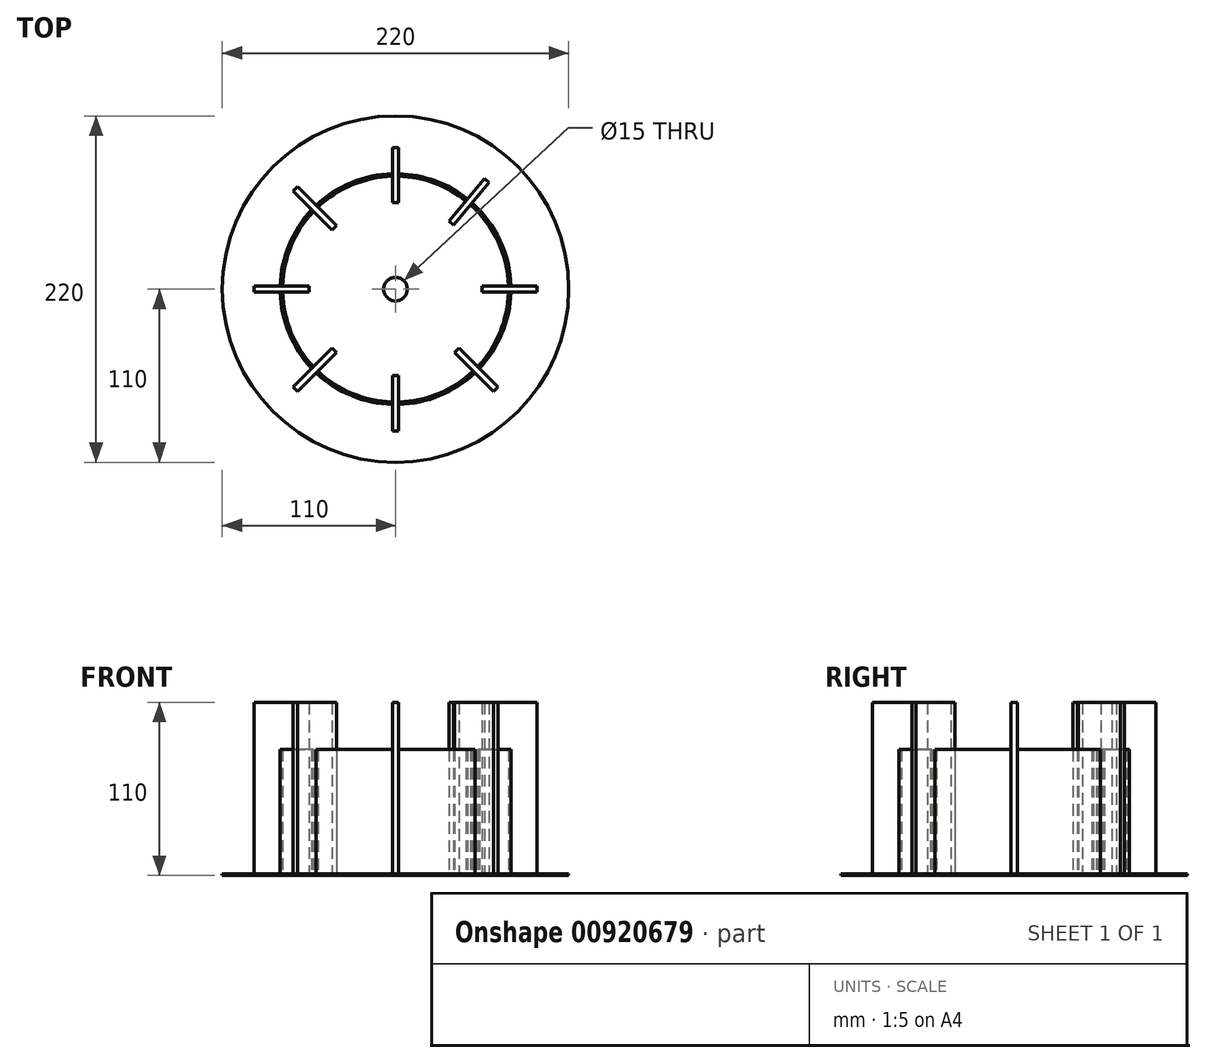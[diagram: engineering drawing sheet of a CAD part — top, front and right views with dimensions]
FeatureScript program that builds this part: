
annotation { "Feature Type Name" : "Feature", "Feature Type Description" : "" }
export const myFeature = defineFeature(function(context is Context, id is Id, definition is map)
    precondition{}
    {
        {
            var Q0;
            Q0=qCreatedBy(makeId("Top.planeOp"),FACE);
            var sketch = newSketch(context, id + "F0", { "sketchPlane" : qUnion([Q0])});
            skCircle(sketch, "E0", {"center": v(0, 0) * mm, "radius": 110 * mm});
            skCircle(sketch, "E1", {"center": v(0, 0) * mm, "radius": 7.5 * mm});
            skLineSegment(sketch, "E2", {"start": v(0, 0) * mm, "end": v(-55, 0) * mm, "construction": true});
            skLineSegment(sketch, "E3", {"start": v(0, 0) * mm, "end": v(55, 0) * mm, "construction": true});
            skLineSegment(sketch, "E4", {"start": v(0, 0) * mm, "end": v(0, -55) * mm, "construction": true});
            skLineSegment(sketch, "E5", {"start": v(0, 0) * mm, "end": v(0, 55) * mm, "construction": true});
            skLineSegment(sketch, "E6", {"start": v(0, 0) * mm, "end": v(-38.9, 38.9) * mm, "construction": true});
            skLineSegment(sketch, "E7", {"start": v(0, 0) * mm, "end": v(3, 3) * mm});
            skLineSegment(sketch, "E8", {"start": v(0, 0) * mm, "end": v(35.45, 42.05) * mm, "construction": true});
            skLineSegment(sketch, "E9", {"start": v(0, 0) * mm, "end": v(38.9, -38.9) * mm, "construction": true});
            skLineSegment(sketch, "E10", {"start": v(0, 0) * mm, "end": v(-38.9, -38.9) * mm, "construction": true});
            skCircle(sketch, "E11", {"center": v(0, 0) * mm, "radius": 55 * mm, "construction": true});
            skCircle(sketch, "E12", {"center": v(0, 0) * mm, "radius": 72.5 * mm, "construction": true});
            skPoint(sketch, "E13", {"position": v(-51.27, 51.27) * mm});
            skPoint(sketch, "E14", {"position": v(0, 72.5) * mm});
            skPoint(sketch, "E15", {"position": v(46.72, 55.44) * mm});
            skPoint(sketch, "E16", {"position": v(72.5, 0) * mm});
            skPoint(sketch, "E17", {"position": v(51.27, -51.27) * mm});
            skPoint(sketch, "E18", {"position": v(0, -72.5) * mm});
            skPoint(sketch, "E19", {"position": v(-51.27, -51.27) * mm});
            skPoint(sketch, "E20", {"position": v(-72.5, 0) * mm});
            skLineSegment(sketch, "E21", {"start": v(-38.9, -38.9) * mm, "end": v(-63.64, -63.64) * mm, "construction": true});
            skLineSegment(sketch, "E22", {"start": v(-63.64, -63.64) * mm, "end": v(-98.46, -98.46) * mm, "construction": true});
            skLineSegment(sketch, "E23", {"start": v(0, -55) * mm, "end": v(0, -90) * mm, "construction": true});
            skLineSegment(sketch, "E24", {"start": v(0, -90) * mm, "end": v(0, -139.25) * mm, "construction": true});
            skLineSegment(sketch, "E25", {"start": v(38.9, -38.9) * mm, "end": v(63.64, -63.64) * mm, "construction": true});
            skLineSegment(sketch, "E26", {"start": v(63.64, -63.64) * mm, "end": v(98.46, -98.46) * mm, "construction": true});
            skLineSegment(sketch, "E27", {"start": v(90, 0) * mm, "end": v(139.25, 0) * mm, "construction": true});
            skLineSegment(sketch, "E28", {"start": v(55, 0) * mm, "end": v(90, 0) * mm, "construction": true});
            skLineSegment(sketch, "E29", {"start": v(58, 68.82) * mm, "end": v(89.74, 106.47) * mm, "construction": true});
            skLineSegment(sketch, "E30", {"start": v(35.45, 42.05) * mm, "end": v(58, 68.82) * mm, "construction": true});
            skLineSegment(sketch, "E31", {"start": v(0, 55) * mm, "end": v(0, 55) * mm});
            skLineSegment(sketch, "E32", {"start": v(0, 90) * mm, "end": v(0, 90) * mm});
            skArc(sketch, "E33", {"start": v(-63.64, 63.64) * mm, "mid": v(34.44, -83.15) * mm, "end": v(0, 90) * mm, "construction": true});
            skLineSegment(sketch, "E34", {"start": v(-38.9, 38.9) * mm, "end": v(-38.9, 38.9) * mm});
            skLineSegment(sketch, "E35", {"start": v(-90, 0) * mm, "end": v(-139.25, 0) * mm, "construction": true});
            skLineSegment(sketch, "E36", {"start": v(-55, 0) * mm, "end": v(-90, 0) * mm, "construction": true});
            skLineSegment(sketch, "E37.0", {"start": v(-55, 2) * mm, "end": v(-90, 2) * mm});
            skLineSegment(sketch, "E38.0", {"start": v(-55, -2) * mm, "end": v(-90, -2) * mm});
            skLineSegment(sketch, "E39", {"start": v(-63.64, 63.64) * mm, "end": v(-63.64, 63.64) * mm});
            skLineSegment(sketch, "E40", {"start": v(-38.9, 38.9) * mm, "end": v(-63.64, 63.64) * mm, "construction": true});
            skLineSegment(sketch, "E41", {"start": v(-63.64, 63.64) * mm, "end": v(-98.46, 98.46) * mm, "construction": true});
            skLineSegment(sketch, "E42.0", {"start": v(-37.48, 40.3) * mm, "end": v(-62.23, 65.05) * mm});
            skLineSegment(sketch, "E43.0", {"start": v(-40.3, 37.48) * mm, "end": v(-65.05, 62.23) * mm});
            skLineSegment(sketch, "E44.0", {"start": v(36.98, 40.77) * mm, "end": v(59.53, 67.53) * mm});
            skLineSegment(sketch, "E45.0", {"start": v(33.92, 43.34) * mm, "end": v(56.47, 70.1) * mm});
            skLineSegment(sketch, "E46.0", {"start": v(55, -2) * mm, "end": v(90, -2) * mm});
            skLineSegment(sketch, "E47.0", {"start": v(55, 2) * mm, "end": v(90, 2) * mm});
            skLineSegment(sketch, "E48.0", {"start": v(37.48, -40.3) * mm, "end": v(62.23, -65.05) * mm});
            skLineSegment(sketch, "E49.0", {"start": v(40.3, -37.48) * mm, "end": v(65.05, -62.23) * mm});
            skLineSegment(sketch, "E50.0", {"start": v(-2, -55) * mm, "end": v(-2, -90) * mm});
            skLineSegment(sketch, "E51.0", {"start": v(2, -55) * mm, "end": v(2, -90) * mm});
            skLineSegment(sketch, "E52.0", {"start": v(-40.3, -37.48) * mm, "end": v(-65.05, -62.23) * mm});
            skLineSegment(sketch, "E53.0", {"start": v(-37.48, -40.3) * mm, "end": v(-62.23, -65.05) * mm});
            skArc(sketch, "E54", {"start": v(0, 90) * mm, "mid": v(-34.44, 83.15) * mm, "end": v(-63.64, 63.64) * mm, "construction": true});
            skLineSegment(sketch, "E55", {"start": v(0, 90) * mm, "end": v(0, 139.25) * mm, "construction": true});
            skLineSegment(sketch, "E56", {"start": v(0, 55) * mm, "end": v(0, 90) * mm, "construction": true});
            skLineSegment(sketch, "E57.0", {"start": v(2, 55) * mm, "end": v(2, 90) * mm});
            skLineSegment(sketch, "E58.0", {"start": v(-2, 55) * mm, "end": v(-2, 90) * mm});
            skLineSegment(sketch, "E59", {"start": v(-2, 90) * mm, "end": v(2, 90) * mm});
            skLineSegment(sketch, "E60", {"start": v(-2, 55) * mm, "end": v(2, 55) * mm});
            skLineSegment(sketch, "E61", {"start": v(56.47, 70.1) * mm, "end": v(59.53, 67.53) * mm});
            skLineSegment(sketch, "E62", {"start": v(33.92, 43.34) * mm, "end": v(36.98, 40.77) * mm});
            skLineSegment(sketch, "E63", {"start": v(55, -2) * mm, "end": v(55, 2) * mm});
            skLineSegment(sketch, "E64", {"start": v(90, 2) * mm, "end": v(90, -2) * mm});
            skLineSegment(sketch, "E65", {"start": v(37.48, -40.3) * mm, "end": v(40.3, -37.48) * mm});
            skLineSegment(sketch, "E66", {"start": v(65.05, -62.23) * mm, "end": v(62.23, -65.05) * mm});
            skLineSegment(sketch, "E67", {"start": v(-2, -55) * mm, "end": v(2, -55) * mm});
            skLineSegment(sketch, "E68", {"start": v(-2, -90) * mm, "end": v(2, -90) * mm});
            skLineSegment(sketch, "E69", {"start": v(-65.05, -62.23) * mm, "end": v(-62.23, -65.05) * mm});
            skLineSegment(sketch, "E70", {"start": v(-40.3, -37.48) * mm, "end": v(-37.48, -40.3) * mm});
            skLineSegment(sketch, "E71", {"start": v(-90, 2) * mm, "end": v(-90, -2) * mm});
            skLineSegment(sketch, "E72", {"start": v(-55, 2) * mm, "end": v(-55, -2) * mm});
            skLineSegment(sketch, "E73", {"start": v(-62.23, 65.05) * mm, "end": v(-65.05, 62.23) * mm});
            skLineSegment(sketch, "E74", {"start": v(-37.48, 40.3) * mm, "end": v(-40.3, 37.48) * mm});
            skCircle(sketch, "E75.0", {"center": v(0, 0) * mm, "radius": 73.3 * mm});
            skCircle(sketch, "E76.0", {"center": v(0, 0) * mm, "radius": 71.7 * mm});
            skSolve(sketch);
        }
        {
            var Q0;
            Q0=makeQuery(id+"F0.imprint","IMPRINT",FACE,{"disambiguationData":[TD([[makeQuery(id+"F0.imprint","IMPRINT",EDGE,{"derivedFrom":sQuery(id+"F0.wireOp",EDGE,"E0")}),1.0]])]});
            var Q1;
            Q1=makeQuery(id+"F0.imprint","IMPRINT",FACE,{"disambiguationData":[TD([[makeQuery(id+"F0.imprint","IMPRINT",EDGE,{"derivedFrom":sQuery(id+"F0.wireOp",EDGE,"E1")}),-1.0]])]});
            extrude(context, id + "F1", {"entities" : qUnion([Q0, Q1]), "depth" : 1 * mm, "offsetDistance" : 25 * mm});
        }
        {
            var Q0;
            Q0=makeQuery(id+"F0.imprint","IMPRINT",FACE,{"disambiguationData":[TD([[makeQuery(id+"F0.imprint","IMPRINT",EDGE,{"derivedFrom":sQuery(id+"F0.wireOp",EDGE,"E37.0")}),1.0]])]});
            var Q1;
            Q1=makeQuery(id+"F0.imprint","IMPRINT",FACE,{"disambiguationData":[TD([[makeQuery(id+"F0.imprint","IMPRINT",EDGE,{"derivedFrom":sQuery(id+"F0.wireOp",EDGE,"E42.0")}),1.0]])]});
            var Q2;
            Q2=makeQuery(id+"F0.imprint","IMPRINT",FACE,{"disambiguationData":[TD([[makeQuery(id+"F0.imprint","IMPRINT",EDGE,{"derivedFrom":sQuery(id+"F0.wireOp",EDGE,"E57.0")}),1.0]])]});
            var Q3;
            Q3=makeQuery(id+"F0.imprint","IMPRINT",FACE,{"disambiguationData":[TD([[makeQuery(id+"F0.imprint","IMPRINT",EDGE,{"derivedFrom":sQuery(id+"F0.wireOp",EDGE,"E44.0")}),1.0]])]});
            var Q4;
            Q4=makeQuery(id+"F0.imprint","IMPRINT",FACE,{"disambiguationData":[TD([[makeQuery(id+"F0.imprint","IMPRINT",EDGE,{"derivedFrom":sQuery(id+"F0.wireOp",EDGE,"E46.0")}),1.0]])]});
            var Q5;
            Q5=makeQuery(id+"F0.imprint","IMPRINT",FACE,{"disambiguationData":[TD([[makeQuery(id+"F0.imprint","IMPRINT",EDGE,{"derivedFrom":sQuery(id+"F0.wireOp",EDGE,"E48.0")}),1.0]])]});
            var Q6;
            Q6=makeQuery(id+"F0.imprint","IMPRINT",FACE,{"disambiguationData":[TD([[makeQuery(id+"F0.imprint","IMPRINT",EDGE,{"derivedFrom":sQuery(id+"F0.wireOp",EDGE,"E50.0")}),1.0]])]});
            var Q7;
            Q7=makeQuery(id+"F0.imprint","IMPRINT",FACE,{"disambiguationData":[TD([[makeQuery(id+"F0.imprint","IMPRINT",EDGE,{"derivedFrom":sQuery(id+"F0.wireOp",EDGE,"E52.0")}),1.0]])]});
            extrude(context, id + "F2", {"entities" : qUnion([Q0, Q1, Q2, Q3, Q4, Q5, Q6, Q7]), "operationType" : NewBodyOperationType.ADD, "depth" : 110 * mm, "offsetDistance" : 25 * mm});
        }
        {
            var Q0;
            {var subQ0=sQuery(id+"F0.wireOp",EDGE,"E76.0");var subQ1=sQuery(id+"F0.wireOp",EDGE,"E37.0");var subQ2=makeQuery(id+"F0.imprint","INTERSECT",VERTEX,{"derivedFrom":[subQ1,subQ0]});Q0=makeQuery(id+"F0.imprint","IMPRINT",FACE,{"disambiguationData":[TD([[makeQuery(id+"F0.imprint","IMPRINT",EDGE,{"disambiguationData":[TD([[subQ2,-1.0]])],"derivedFrom":subQ1}),-1.0]])]});}
            var Q1;
            {var subQ0=sQuery(id+"F0.wireOp",EDGE,"E76.0");var subQ1=sQuery(id+"F0.wireOp",EDGE,"E42.0");var subQ2=makeQuery(id+"F0.imprint","INTERSECT",VERTEX,{"derivedFrom":[subQ1,subQ0]});Q1=makeQuery(id+"F0.imprint","IMPRINT",FACE,{"disambiguationData":[TD([[makeQuery(id+"F0.imprint","IMPRINT",EDGE,{"disambiguationData":[TD([[subQ2,-1.0]])],"derivedFrom":subQ1}),-1.0]])]});}
            var Q2;
            {var subQ0=sQuery(id+"F0.wireOp",EDGE,"E76.0");var subQ1=sQuery(id+"F0.wireOp",EDGE,"E45.0");var subQ2=makeQuery(id+"F0.imprint","INTERSECT",VERTEX,{"derivedFrom":[subQ1,subQ0]});Q2=makeQuery(id+"F0.imprint","IMPRINT",FACE,{"disambiguationData":[TD([[makeQuery(id+"F0.imprint","IMPRINT",EDGE,{"disambiguationData":[TD([[subQ2,-1.0]])],"derivedFrom":subQ1}),1.0]])]});}
            var Q3;
            {var subQ0=sQuery(id+"F0.wireOp",EDGE,"E76.0");var subQ1=sQuery(id+"F0.wireOp",EDGE,"E44.0");var subQ2=makeQuery(id+"F0.imprint","INTERSECT",VERTEX,{"derivedFrom":[subQ1,subQ0]});Q3=makeQuery(id+"F0.imprint","IMPRINT",FACE,{"disambiguationData":[TD([[makeQuery(id+"F0.imprint","IMPRINT",EDGE,{"disambiguationData":[TD([[subQ2,-1.0]])],"derivedFrom":subQ1}),-1.0]])]});}
            var Q4;
            {var subQ0=sQuery(id+"F0.wireOp",EDGE,"E76.0");var subQ1=sQuery(id+"F0.wireOp",EDGE,"E46.0");var subQ2=makeQuery(id+"F0.imprint","INTERSECT",VERTEX,{"derivedFrom":[subQ1,subQ0]});Q4=makeQuery(id+"F0.imprint","IMPRINT",FACE,{"disambiguationData":[TD([[makeQuery(id+"F0.imprint","IMPRINT",EDGE,{"disambiguationData":[TD([[subQ2,-1.0]])],"derivedFrom":subQ1}),-1.0]])]});}
            var Q5;
            {var subQ0=sQuery(id+"F0.wireOp",EDGE,"E76.0");var subQ1=sQuery(id+"F0.wireOp",EDGE,"E48.0");var subQ2=makeQuery(id+"F0.imprint","INTERSECT",VERTEX,{"derivedFrom":[subQ1,subQ0]});Q5=makeQuery(id+"F0.imprint","IMPRINT",FACE,{"disambiguationData":[TD([[makeQuery(id+"F0.imprint","IMPRINT",EDGE,{"disambiguationData":[TD([[subQ2,-1.0]])],"derivedFrom":subQ1}),-1.0]])]});}
            var Q6;
            {var subQ0=sQuery(id+"F0.wireOp",EDGE,"E76.0");var subQ1=sQuery(id+"F0.wireOp",EDGE,"E50.0");var subQ2=makeQuery(id+"F0.imprint","INTERSECT",VERTEX,{"derivedFrom":[subQ1,subQ0]});Q6=makeQuery(id+"F0.imprint","IMPRINT",FACE,{"disambiguationData":[TD([[makeQuery(id+"F0.imprint","IMPRINT",EDGE,{"disambiguationData":[TD([[subQ2,-1.0]])],"derivedFrom":subQ1}),-1.0]])]});}
            var Q7;
            {var subQ0=sQuery(id+"F0.wireOp",EDGE,"E76.0");var subQ1=sQuery(id+"F0.wireOp",EDGE,"E38.0");var subQ2=makeQuery(id+"F0.imprint","INTERSECT",VERTEX,{"derivedFrom":[subQ1,subQ0]});Q7=makeQuery(id+"F0.imprint","IMPRINT",FACE,{"disambiguationData":[TD([[makeQuery(id+"F0.imprint","IMPRINT",EDGE,{"disambiguationData":[TD([[subQ2,-1.0]])],"derivedFrom":subQ1}),1.0]])]});}
            extrude(context, id + "F3", {"entities" : qUnion([Q0, Q1, Q2, Q3, Q4, Q5, Q6, Q7]), "operationType" : NewBodyOperationType.ADD, "depth" : 80 * mm, "offsetDistance" : 25 * mm});
        }
    });
